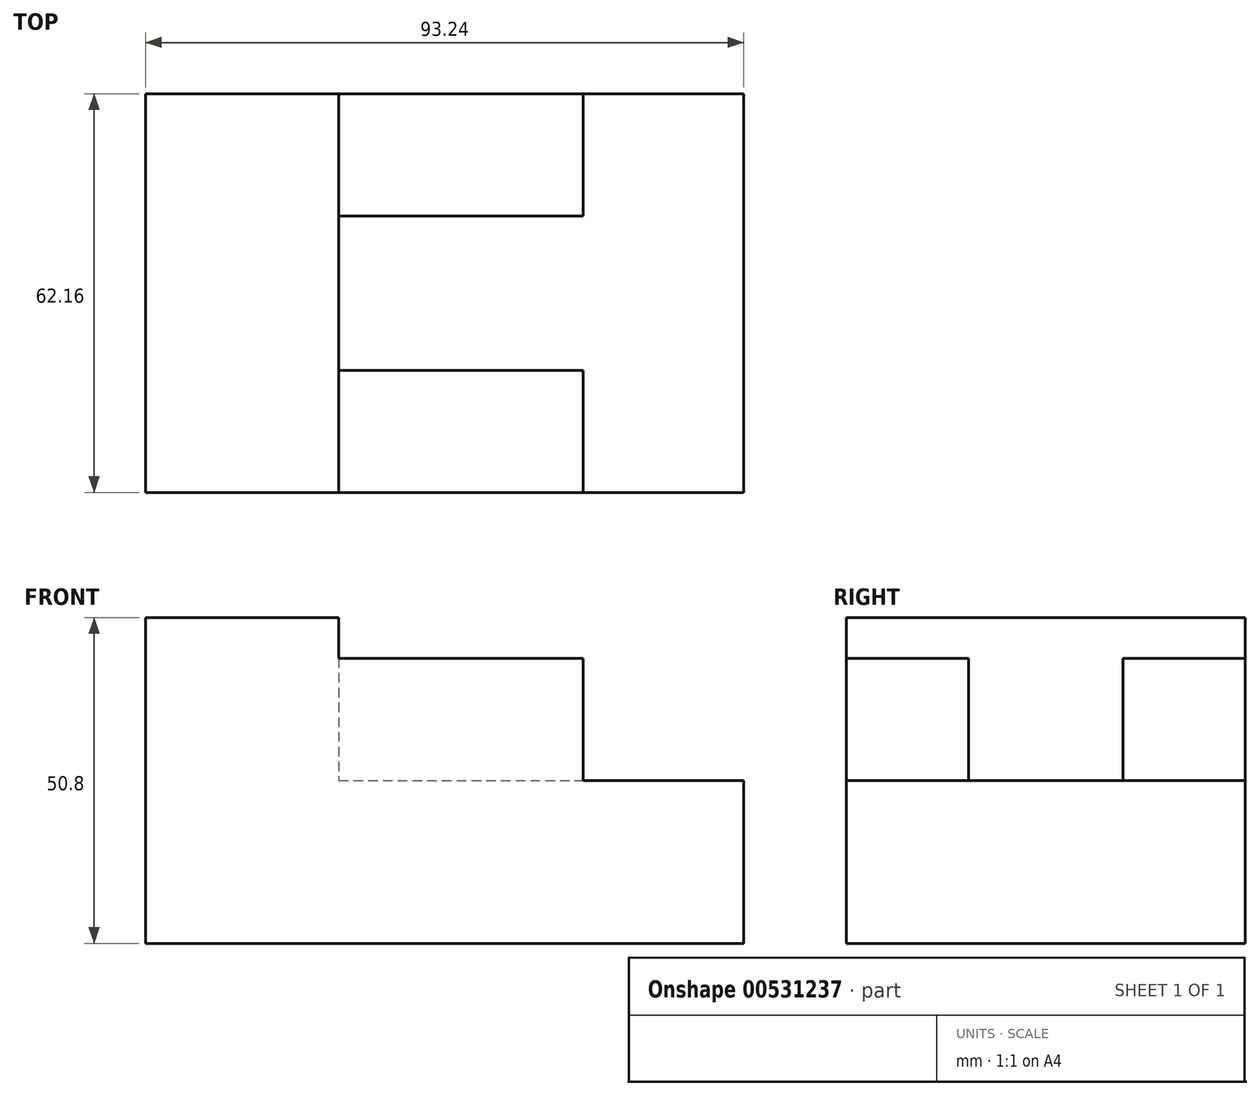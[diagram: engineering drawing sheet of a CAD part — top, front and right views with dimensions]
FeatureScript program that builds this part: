
annotation { "Feature Type Name" : "Feature", "Feature Type Description" : "" }
export const myFeature = defineFeature(function(context is Context, id is Id, definition is map)
    precondition{}
    {
        {
            var Q0;
            Q0=qCreatedBy(makeId("Top.planeOp"),FACE);
            var sketch = newSketch(context, id + "F0", { "sketchPlane" : qUnion([Q0])});
            skLineSegment(sketch, "E0.bottom", {"start": v(46.62, 31.08) * mm, "end": v(-46.62, 31.08) * mm});
            skLineSegment(sketch, "E0.top", {"start": v(46.62, -31.08) * mm, "end": v(-46.62, -31.08) * mm});
            skLineSegment(sketch, "E0.left", {"start": v(46.62, 31.08) * mm, "end": v(46.62, -31.08) * mm});
            skLineSegment(sketch, "E0.right", {"start": v(-46.62, 31.08) * mm, "end": v(-46.62, -31.08) * mm});
            skPoint(sketch, "E0.middle", {"position": v(0, 0) * mm});
            skSolve(sketch);
        }
        {
            var Q0;
            Q0=makeQuery(id+"F0.imprint","IMPRINT",FACE,{"disambiguationData":[TD([[makeQuery(id+"F0.imprint","IMPRINT",EDGE,{"derivedFrom":sQuery(id+"F0.wireOp",EDGE,"E0.bottom")}),1.0]])]});
            extrude(context, id + "F1", {"entities" : qUnion([Q0]), "depth" : 25.4 * mm, "offsetDistance" : 25.4 * mm});
        }
        {
            var Q0;
            Q0=makeQuery(id+"F1.opExtrude","CAP_FACE",FACE,{"disambiguationData":[OSD([sQuery(id+"F0.wireOp",EDGE,"E0.bottom"),sQuery(id+"F0.wireOp",EDGE,"E0.top"),sQuery(id+"F0.wireOp",EDGE,"E0.left"),sQuery(id+"F0.wireOp",EDGE,"E0.right")])],"isStart":false});
            var sketch = newSketch(context, id + "F2", { "sketchPlane" : qUnion([Q0])});
            skLineSegment(sketch, "E1.bottom", {"start": v(-46.62, 31.08) * mm, "end": v(-16.5, 31.08) * mm});
            skLineSegment(sketch, "E1.top", {"start": v(-46.62, -31.08) * mm, "end": v(-16.5, -31.08) * mm});
            skLineSegment(sketch, "E1.left", {"start": v(-46.62, 31.08) * mm, "end": v(-46.62, -31.08) * mm});
            skLineSegment(sketch, "E1.right", {"start": v(-16.5, 31.08) * mm, "end": v(-16.5, -31.08) * mm});
            skSolve(sketch);
        }
        {
            var Q0;
            Q0 = qSketchRegion(id + "F2", true);
            extrude(context, id + "F3", {"entities" : qUnion([Q0]), "operationType" : NewBodyOperationType.ADD, "depth" : 25.4 * mm, "offsetDistance" : 25.4 * mm});
        }
        {
            var Q0;
            Q0=makeQuery(id+"F1.opExtrude","CAP_FACE",FACE,{"disambiguationData":[OSD([sQuery(id+"F0.wireOp",EDGE,"E0.bottom"),sQuery(id+"F0.wireOp",EDGE,"E0.top"),sQuery(id+"F0.wireOp",EDGE,"E0.left"),sQuery(id+"F0.wireOp",EDGE,"E0.right")])],"isStart":false});
            var sketch = newSketch(context, id + "F4", { "sketchPlane" : qUnion([Q0])});
            skLineSegment(sketch, "E2.bottom", {"start": v(-16.5, 31.08) * mm, "end": v(21.6, 31.08) * mm});
            skLineSegment(sketch, "E2.top", {"start": v(-16.5, 12.03) * mm, "end": v(21.6, 12.03) * mm});
            skLineSegment(sketch, "E2.left", {"start": v(-16.5, 31.08) * mm, "end": v(-16.5, 12.03) * mm});
            skLineSegment(sketch, "E2.right", {"start": v(21.6, 31.08) * mm, "end": v(21.6, 12.03) * mm});
            skLineSegment(sketch, "E3.bottom", {"start": v(-16.5, -31.08) * mm, "end": v(21.6, -31.08) * mm});
            skLineSegment(sketch, "E3.top", {"start": v(-16.5, -12.03) * mm, "end": v(21.6, -12.03) * mm});
            skLineSegment(sketch, "E3.left", {"start": v(-16.5, -31.08) * mm, "end": v(-16.5, -12.03) * mm});
            skLineSegment(sketch, "E3.right", {"start": v(21.6, -31.08) * mm, "end": v(21.6, -12.03) * mm});
            skSolve(sketch);
        }
        {
            var Q0;
            Q0 = qSketchRegion(id + "F4", true);
            extrude(context, id + "F5", {"entities" : qUnion([Q0]), "operationType" : NewBodyOperationType.ADD, "depth" : 19.05 * mm, "offsetDistance" : 25.4 * mm});
        }
    });
